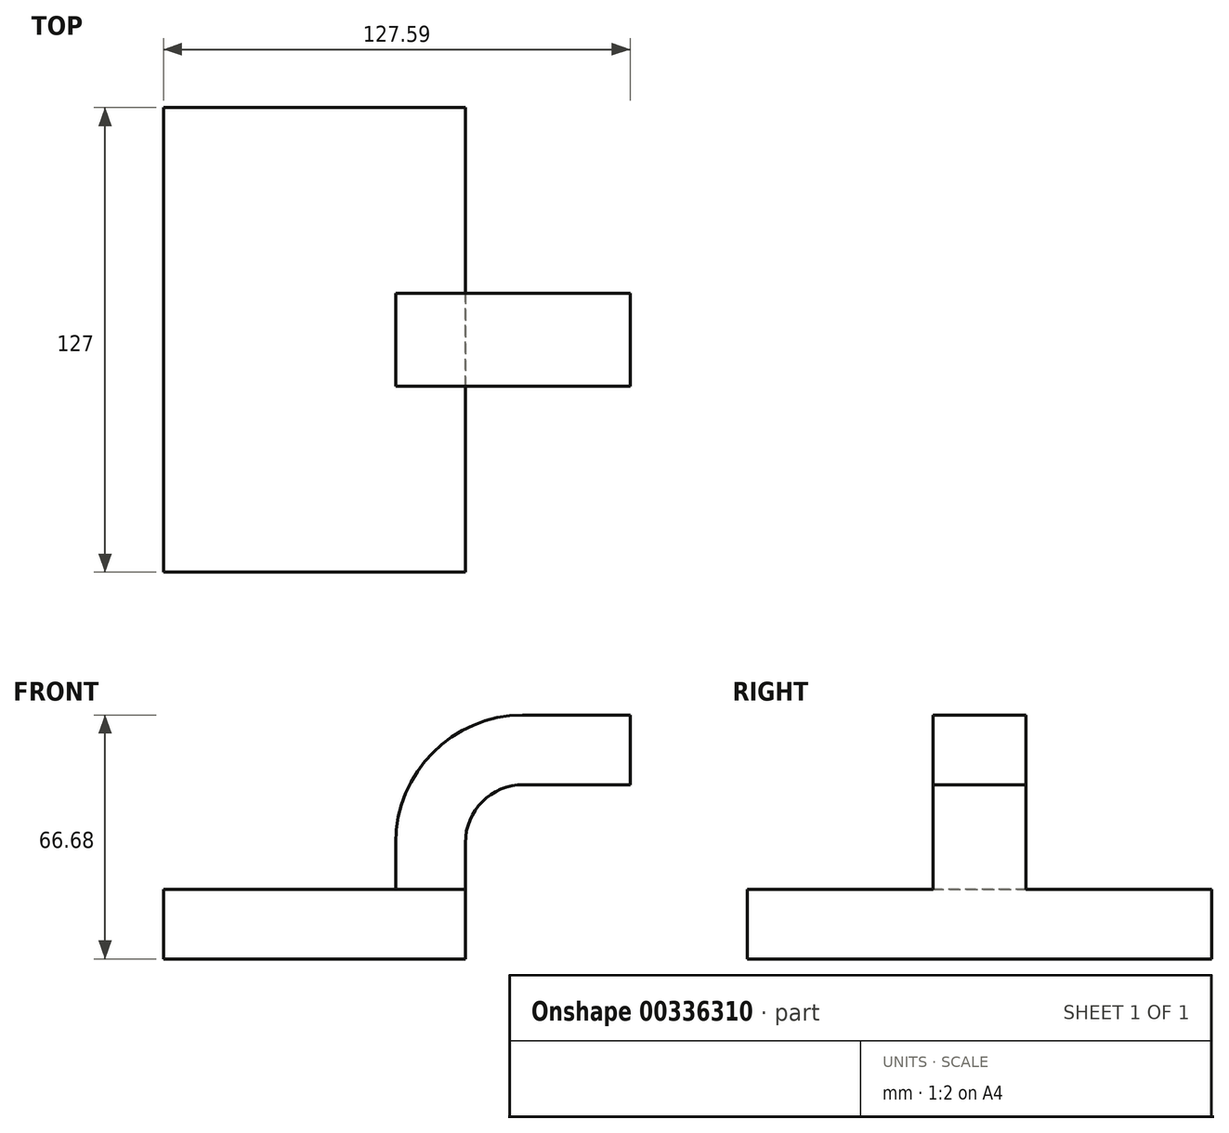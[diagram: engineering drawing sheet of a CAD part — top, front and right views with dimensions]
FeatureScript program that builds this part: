
annotation { "Feature Type Name" : "Feature", "Feature Type Description" : "" }
export const myFeature = defineFeature(function(context is Context, id is Id, definition is map)
    precondition{}
    {
        {
            var Q0;
            Q0=qCreatedBy(makeId("Front.planeOp"),FACE);
            var sketch = newSketch(context, id + "F0", { "sketchPlane" : qUnion([Q0])});
            skLineSegment(sketch, "E0.bottom", {"start": v(-41.28, -9.53) * mm, "end": v(41.28, -9.53) * mm});
            skLineSegment(sketch, "E0.top", {"start": v(-41.28, 9.53) * mm, "end": v(41.28, 9.53) * mm});
            skLineSegment(sketch, "E0.left", {"start": v(-41.28, -9.53) * mm, "end": v(-41.28, 9.53) * mm});
            skLineSegment(sketch, "E0.right", {"start": v(41.28, -9.53) * mm, "end": v(41.28, 9.53) * mm});
            skPoint(sketch, "E0.middle", {"position": v(0, 0) * mm});
            skLineSegment(sketch, "E1", {"start": v(41.28, 9.53) * mm, "end": v(41.28, 22.23) * mm});
            skArc(sketch, "E2", {"start": v(41.27, 22.23) * mm, "mid": v(45.92, 33.45) * mm, "end": v(57.15, 38.1) * mm});
            skLineSegment(sketch, "E3.bottom", {"start": v(61.21, 34.01) * mm, "end": v(112.01, 34.01) * mm});
            skLineSegment(sketch, "E3.top", {"start": v(61.21, 62.59) * mm, "end": v(112.01, 62.59) * mm});
            skLineSegment(sketch, "E3.left", {"start": v(61.21, 34.01) * mm, "end": v(61.21, 62.59) * mm});
            skLineSegment(sketch, "E3.right", {"start": v(112.01, 34.01) * mm, "end": v(112.01, 62.59) * mm});
            skPoint(sketch, "E3.middle", {"position": v(86.61, 48.3) * mm});
            skLineSegment(sketch, "E4", {"start": v(57.15, 38.1) * mm, "end": v(86.31, 38.1) * mm});
            skLineSegment(sketch, "E5.0", {"start": v(57.15, 57.15) * mm, "end": v(86.31, 57.15) * mm});
            skArc(sketch, "E5.1", {"start": v(22.23, 22.23) * mm, "mid": v(32.45, 46.92) * mm, "end": v(57.15, 57.15) * mm});
            skLineSegment(sketch, "E5.2", {"start": v(22.23, 9.53) * mm, "end": v(22.23, 22.23) * mm});
            skFitSpline(sketch, "E6", {"points": [v(-41.28, 9.53) * mm, v(57.15, 57.15) * mm], "startDerivative": vector(1.12, 69.82) * mm, "endDerivative": vector(146.14, 0.36) * mm});
            skLineSegment(sketch, "E7", {"start": v(86.31, 57.15) * mm, "end": v(86.31, 38.1) * mm});
            skSolve(sketch);
        }
        {
            var Q0;
            Q0=makeQuery(id+"F0.imprint","IMPRINT",FACE,{"disambiguationData":[TD([[makeQuery(id+"F0.imprint","IMPRINT",EDGE,{"derivedFrom":sQuery(id+"F0.wireOp",EDGE,"E0.bottom")}),1.0]])]});
            extrude(context, id + "F1", {"entities" : qUnion([Q0]), "endBound" : BoundingType.SYMMETRIC, "oppositeDirection" : true, "depth" : 127 * mm});
        }
        {
            var Q0;
            {var subQ7=sQuery(id+"F0.wireOp",EDGE,"E1");Q0=makeQuery(id+"F0.imprint","IMPRINT",FACE,{"disambiguationData":[TD([[makeQuery(id+"F0.imprint","IMPRINT",EDGE,{"derivedFrom":subQ7}),1.0]])]});}
            var Q1;
            {var subQ5=sQuery(id+"F0.wireOp",EDGE,"E7");Q1=makeQuery(id+"F0.imprint","IMPRINT",FACE,{"disambiguationData":[TD([[makeQuery(id+"F0.imprint","IMPRINT",EDGE,{"derivedFrom":subQ5}),-1.0]])]});}
            extrude(context, id + "F2", {"entities" : qUnion([Q0, Q1]), "operationType" : NewBodyOperationType.ADD, "endBound" : BoundingType.SYMMETRIC, "depth" : 25.4 * mm});
        }
        {
            var Q0;
            Q0=makeQuery(id+"F0.imprint","IMPRINT",FACE,{"disambiguationData":[TD([[makeQuery(id+"F0.imprint","IMPRINT",EDGE,{"derivedFrom":sQuery(id+"F0.wireOp",EDGE,"E5.1")}),1.0]])]});
            extrude(context, id + "F3", {"entities" : qUnion([Q0]), "operationType" : NewBodyOperationType.ADD, "endBound" : BoundingType.SYMMETRIC, "depth" : 15.88 * mm});
        }
    });
